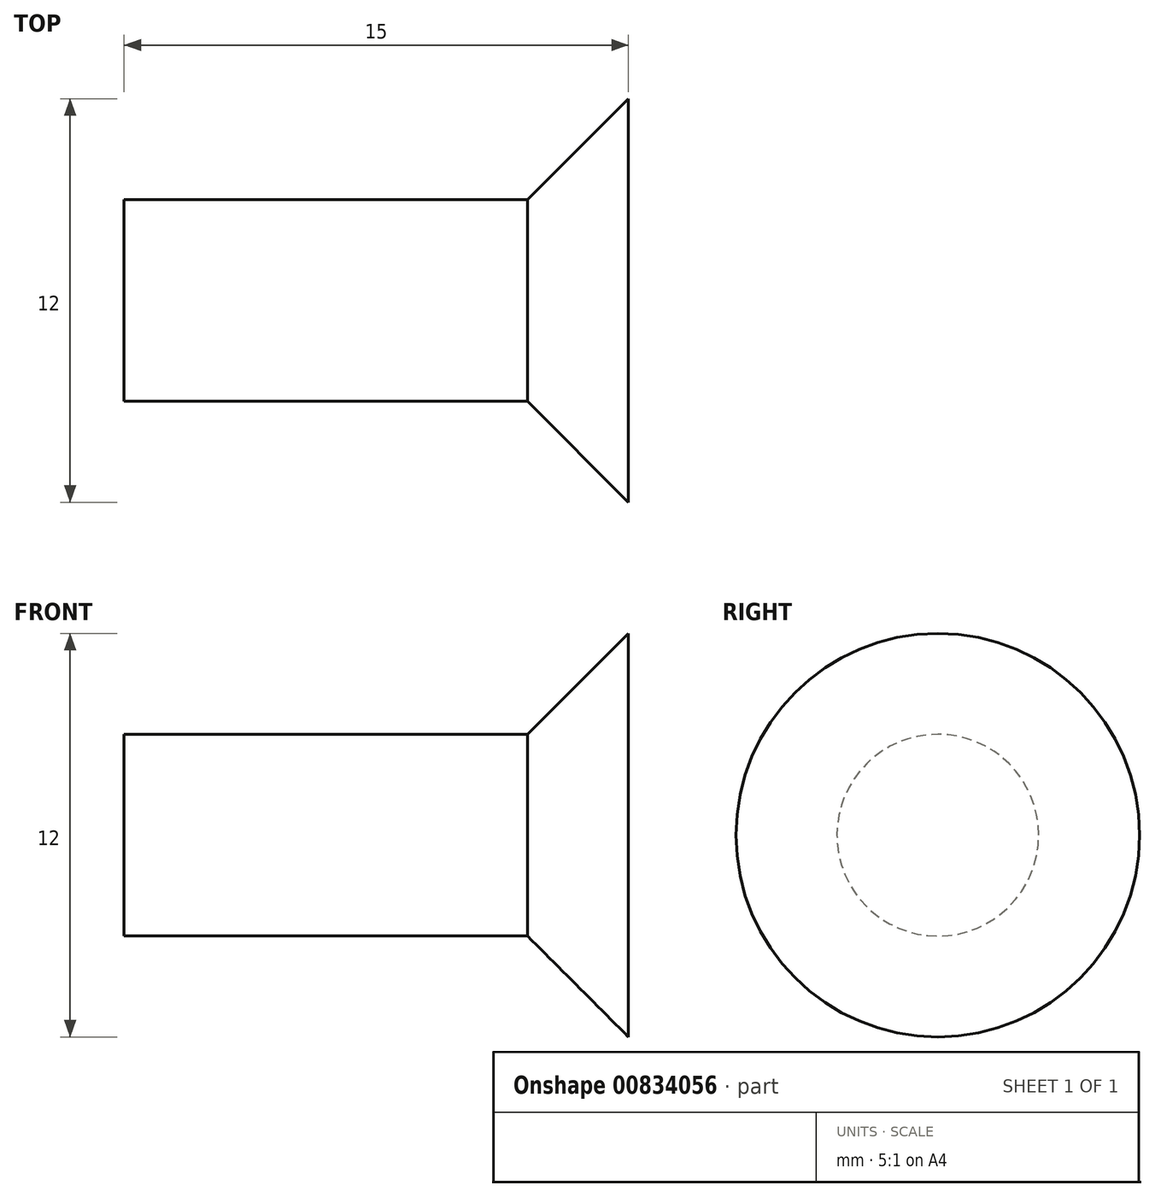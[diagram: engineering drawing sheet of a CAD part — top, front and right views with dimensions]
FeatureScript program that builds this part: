
annotation { "Feature Type Name" : "Feature", "Feature Type Description" : "" }
export const myFeature = defineFeature(function(context is Context, id is Id, definition is map)
    precondition{}
    {
        {
            var Q0;
            Q0=qCreatedBy(makeId("Right.planeOp"),FACE);
            var sketch = newSketch(context, id + "F0", { "sketchPlane" : qUnion([Q0])});
            skCircle(sketch, "E0", {"center": v(0, 0) * mm, "radius": 3 * mm});
            skSolve(sketch);
        }
        {
            var Q0;
            Q0 = qSketchRegion(id + "F0", true);
            extrude(context, id + "F1", {"entities" : qUnion([Q0]), "depth" : 15 * mm, "offsetDistance" : 25 * mm});
        }
        {
            var Q0;
            Q0=makeQuery(id+"F1.opExtrude","CAP_FACE",FACE,{"disambiguationData":[OSD([sQuery(id+"F0.wireOp",EDGE,"E0")])],"isStart":false});
            var sketch = newSketch(context, id + "F2", { "sketchPlane" : qUnion([Q0])});
            skCircle(sketch, "E1", {"center": v(0, 0) * mm, "radius": 6 * mm});
            skSolve(sketch);
        }
        {
            var Q0;
            Q0=makeQuery(id+"F2.imprint","IMPRINT",FACE,{"disambiguationData":[TD([[makeQuery(id+"F2.imprint","IMPRINT",EDGE,{"derivedFrom":sQuery(id+"F2.wireOp",EDGE,"E1")}),1.0]])]});
            extrude(context, id + "F3", {"entities" : qUnion([Q0]), "operationType" : NewBodyOperationType.ADD, "oppositeDirection" : true, "depth" : 3 * mm, "offsetDistance" : 25 * mm});
        }
        {
            var Q0;
            Q0=makeQuery(id+"F3.opExtrude","CAP_EDGE",EDGE,{"disambiguationData":[OSD([sQuery(id+"F2.wireOp",EDGE,"E1")])],"isStart":false});
            chamfer(context, id + "F4", {"entities" : qUnion([Q0]), "width" : 3 * mm, "tangentPropagation" : true});
        }
    });
